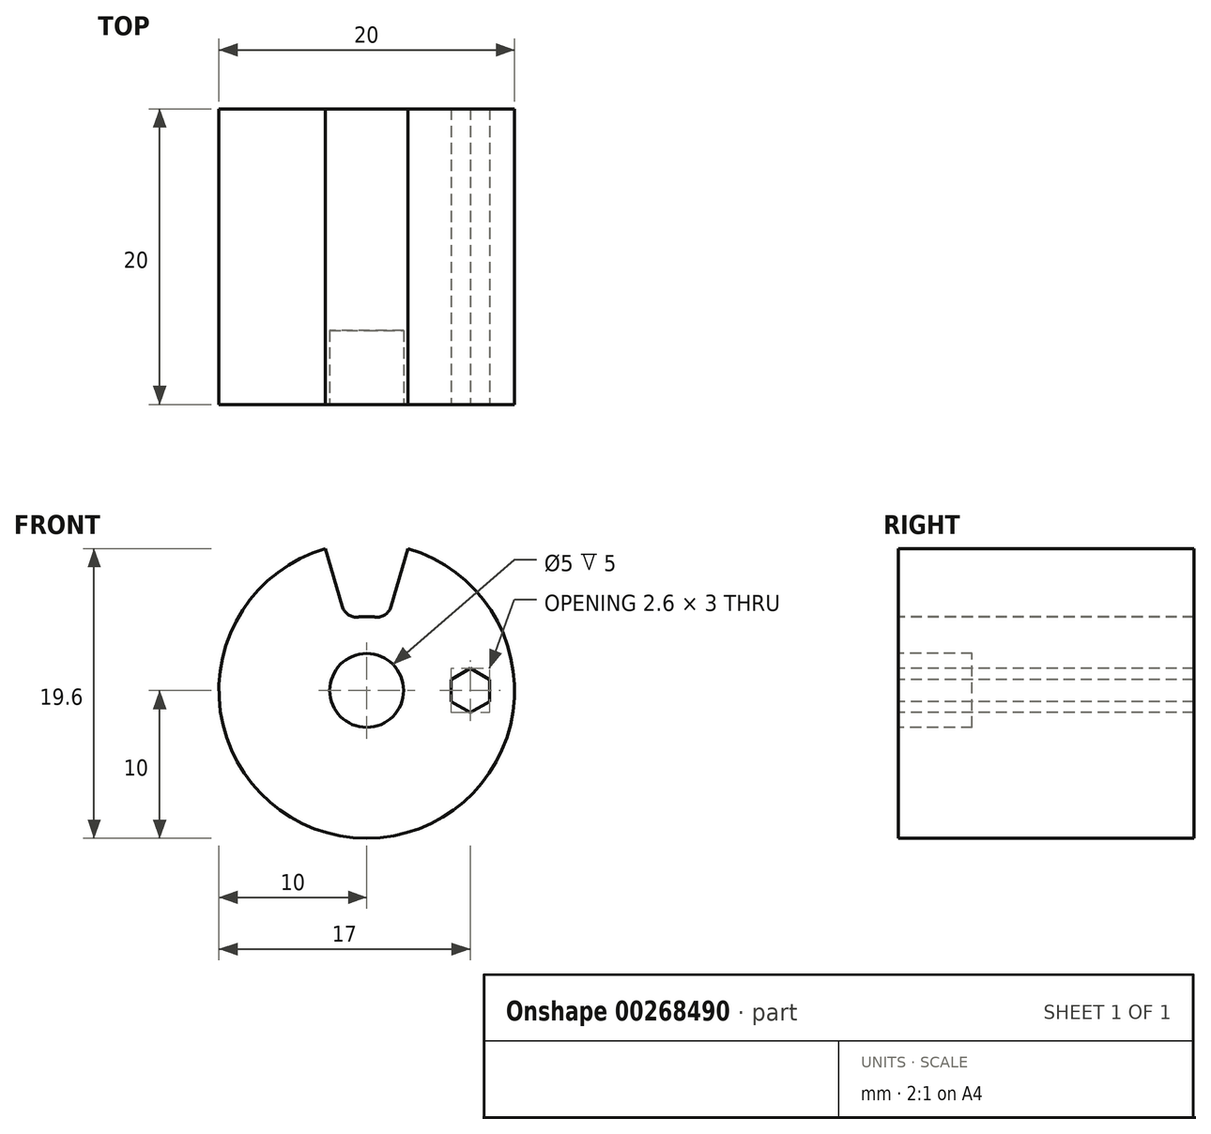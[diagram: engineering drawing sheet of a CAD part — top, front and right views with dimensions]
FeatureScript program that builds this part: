
annotation { "Feature Type Name" : "Feature", "Feature Type Description" : "" }
export const myFeature = defineFeature(function(context is Context, id is Id, definition is map)
    precondition{}
    {
        {
            var Q0;
            Q0=qCreatedBy(makeId("Front.planeOp"),FACE);
            var sketch = newSketch(context, id + "F0", { "sketchPlane" : qUnion([Q0])});
            skCircle(sketch, "E0", {"center": v(0, 0) * mm, "radius": 10 * mm});
            skSolve(sketch);
        }
        {
            var Q0;
            Q0=makeQuery(id+"F0.imprint","IMPRINT",FACE,{"disambiguationData":[TD([[makeQuery(id+"F0.imprint","IMPRINT",EDGE,{"derivedFrom":sQuery(id+"F0.wireOp",EDGE,"E0")}),1.0]])]});
            extrude(context, id + "F1", {"entities" : qUnion([Q0]), "depth" : 20 * mm});
        }
        {
            var Q0;
            Q0=makeQuery(id+"F1.opExtrude","CAP_FACE",FACE,{"disambiguationData":[OSD([sQuery(id+"F0.wireOp",EDGE,"E0")])],"isStart":false});
            var sketch = newSketch(context, id + "F2", { "sketchPlane" : qUnion([Q0])});
            skCircle(sketch, "E1", {"center": v(0, 0) * mm, "radius": 2.5 * mm});
            skSolve(sketch);
        }
        {
            var Q0;
            Q0=makeQuery(id+"F2.imprint","IMPRINT",FACE,{"disambiguationData":[TD([[makeQuery(id+"F2.imprint","IMPRINT",EDGE,{"derivedFrom":sQuery(id+"F2.wireOp",EDGE,"E1")}),1.0]])]});
            var Q1;
            Q1=sQuery(id+"F2.wireOp",EDGE,"E1");
            extrude(context, id + "F3", {"entities" : qUnion([Q0]), "operationType" : NewBodyOperationType.REMOVE, "surfaceEntities" : qUnion([Q1]), "oppositeDirection" : true, "depth" : 5 * mm});
        }
        {
            var Q0;
            Q0=makeQuery(id+"F1.opExtrude","CAP_FACE",FACE,{"disambiguationData":[OSD([sQuery(id+"F0.wireOp",EDGE,"E0")])],"isStart":false});
            var sketch = newSketch(context, id + "F12", { "sketchPlane" : qUnion([Q0])});
            skLineSegment(sketch, "E2", {"start": v(0, 0) * mm, "end": v(0, 10) * mm, "construction": true});
            skLineSegment(sketch, "E3", {"start": v(0, 10) * mm, "end": v(0, 0) * mm});
            skLineSegment(sketch, "E4", {"start": v(1.4, 4.8) * mm, "end": v(2.8, 9.6) * mm});
            skLineSegment(sketch, "E5", {"start": v(-1.4, 4.8) * mm, "end": v(-2.8, 9.6) * mm});
            skArc(sketch, "E6", {"start": v(2.8, 9.6) * mm, "mid": v(0, 10) * mm, "end": v(-2.8, 9.6) * mm});
            skArc(sketch, "E7", {"start": v(1.4, 4.8) * mm, "mid": v(0, 5) * mm, "end": v(-1.4, 4.8) * mm});
            skSolve(sketch);
        }
        {
            var Q0;
            {var subQ5=sQuery(id+"F12.wireOp",EDGE,"E4");Q0=makeQuery(id+"F12.imprint","IMPRINT",FACE,{"disambiguationData":[TD([[makeQuery(id+"F12.imprint","IMPRINT",EDGE,{"derivedFrom":subQ5}),1.0]])]});}
            var Q1;
            {var subQ5=sQuery(id+"F12.wireOp",EDGE,"E5");Q1=makeQuery(id+"F12.imprint","IMPRINT",FACE,{"disambiguationData":[TD([[makeQuery(id+"F12.imprint","IMPRINT",EDGE,{"derivedFrom":subQ5}),-1.0]])]});}
            extrude(context, id + "F13", {"entities" : qUnion([Q0, Q1]), "operationType" : NewBodyOperationType.REMOVE, "endBound" : BoundingType.THROUGH_ALL, "oppositeDirection" : true, "depth" : 25 * mm});
        }
        {
            var Q0;
            Q0=makeQuery(id+"F13.boolean.opBoolean","COPY",EDGE,{"derivedFrom":makeQuery(id+"F13.opExtrude","SWEPT_EDGE",EDGE,{"disambiguationData":[OSD([sQuery(id+"F0.wireOp",EDGE,"E0"),sQuery(id+"F12.wireOp",EDGE,"E5"),sQuery(id+"F12.wireOp",EDGE,"E6")])]})});
            var Q1;
            Q1=makeQuery(id+"F13.boolean.opBoolean","COPY",EDGE,{"derivedFrom":makeQuery(id+"F13.opExtrude","SWEPT_EDGE",EDGE,{"disambiguationData":[OSD([sQuery(id+"F0.wireOp",EDGE,"E0"),sQuery(id+"F12.wireOp",EDGE,"E4"),sQuery(id+"F12.wireOp",EDGE,"E6")])]})});
            var Q2;
            Q2=makeQuery(id+"F13.boolean.opBoolean","COPY",EDGE,{"derivedFrom":makeQuery(id+"F13.opExtrude","SWEPT_EDGE",EDGE,{"disambiguationData":[OSD([sQuery(id+"F12.wireOp",EDGE,"E5"),sQuery(id+"F12.wireOp",EDGE,"E7")])]})});
            var Q3;
            Q3=makeQuery(id+"F13.boolean.opBoolean","COPY",EDGE,{"derivedFrom":makeQuery(id+"F13.opExtrude","SWEPT_EDGE",EDGE,{"disambiguationData":[OSD([sQuery(id+"F12.wireOp",EDGE,"E4"),sQuery(id+"F12.wireOp",EDGE,"E7")])]})});
            fillet(context, id + "F4", {"entities" : qUnion([Q0, Q1, Q2, Q3]), "radius" : 1 * mm, "tangentPropagation" : true, "allowEdgeOverflow" : false});
        }
        {
            var Q0;
            Q0=makeQuery(id+"F1.opExtrude","CAP_FACE",FACE,{"disambiguationData":[OSD([sQuery(id+"F0.wireOp",EDGE,"E0")])],"isStart":false});
            var sketch = newSketch(context, id + "F5", { "sketchPlane" : qUnion([Q0])});
            skCircle(sketch, "E8.cCircle", {"center": v(7, 0) * mm, "radius": 1.5 * mm, "construction": true});
            skLineSegment(sketch, "E8.0", {"start": v(7, 1.5) * mm, "end": v(8.3, 0.75) * mm});
            skLineSegment(sketch, "E8.1", {"start": v(8.3, 0.75) * mm, "end": v(8.3, -0.75) * mm});
            skLineSegment(sketch, "E8.2", {"start": v(8.3, -0.75) * mm, "end": v(7, -1.5) * mm});
            skLineSegment(sketch, "E8.3", {"start": v(7, -1.5) * mm, "end": v(5.7, -0.75) * mm});
            skLineSegment(sketch, "E8.4", {"start": v(5.7, -0.75) * mm, "end": v(5.7, 0.75) * mm});
            skLineSegment(sketch, "E8.5", {"start": v(5.7, 0.75) * mm, "end": v(7, 1.5) * mm});
            skLineSegment(sketch, "E9", {"start": v(7, -1.5) * mm, "end": v(7, 1.5) * mm, "construction": true});
            skLineSegment(sketch, "E10", {"start": v(7, 0) * mm, "end": v(0, 0) * mm, "construction": true});
            skSolve(sketch);
        }
        {
            var Q0;
            Q0=makeQuery(id+"F5.imprint","IMPRINT",FACE,{"disambiguationData":[TD([[makeQuery(id+"F5.imprint","IMPRINT",EDGE,{"derivedFrom":sQuery(id+"F5.wireOp",EDGE,"E8.0")}),-1.0]])]});
            extrude(context, id + "F6", {"entities" : qUnion([Q0]), "operationType" : NewBodyOperationType.REMOVE, "endBound" : BoundingType.THROUGH_ALL, "oppositeDirection" : true, "depth" : 25 * mm});
        }
        {
            var Q0;
            Q0=makeQuery(id+"F1.opExtrude","CAP_FACE",FACE,{"disambiguationData":[OSD([sQuery(id+"F0.wireOp",EDGE,"E0")])],"isStart":false});
            var sketch = newSketch(context, id + "F7", { "sketchPlane" : qUnion([Q0])});
            skCircle(sketch, "E11", {"center": v(-6.95, 0.84) * mm, "radius": 3 * mm});
            skSolve(sketch);
        }
        {
            var Q0;
            Q0=sQuery(id+"F7.wireOp",EDGE,"E11");
            extrude(context, id + "F8", {"bodyType" : ToolBodyType.SURFACE, "surfaceEntities" : qUnion([Q0]), "depth" : 25 * mm});
        }
        {
            var Q0;
            Q0=makeQuery(id+"F1.opExtrude","CAP_FACE",FACE,{"disambiguationData":[OSD([sQuery(id+"F0.wireOp",EDGE,"E0")])],"isStart":true});
            var sketch = newSketch(context, id + "F9", { "sketchPlane" : qUnion([Q0])});
            skCircle(sketch, "E12", {"center": v(11.77, -20.38) * mm, "radius": 5.32 * mm});
            skSolve(sketch);
        }
        {
            var Q0;
            Q0=makeQuery(id+"F9.imprint","IMPRINT",FACE,{"disambiguationData":[TD([[makeQuery(id+"F9.imprint","IMPRINT",EDGE,{"derivedFrom":sQuery(id+"F9.wireOp",EDGE,"E12")}),1.0]])]});
            extrude(context, id + "F10", {"entities" : qUnion([Q0]), "operationType" : NewBodyOperationType.REMOVE, "oppositeDirection" : true, "depth" : 25 * mm, "offsetDistance" : 25 * mm});
        }
    });
